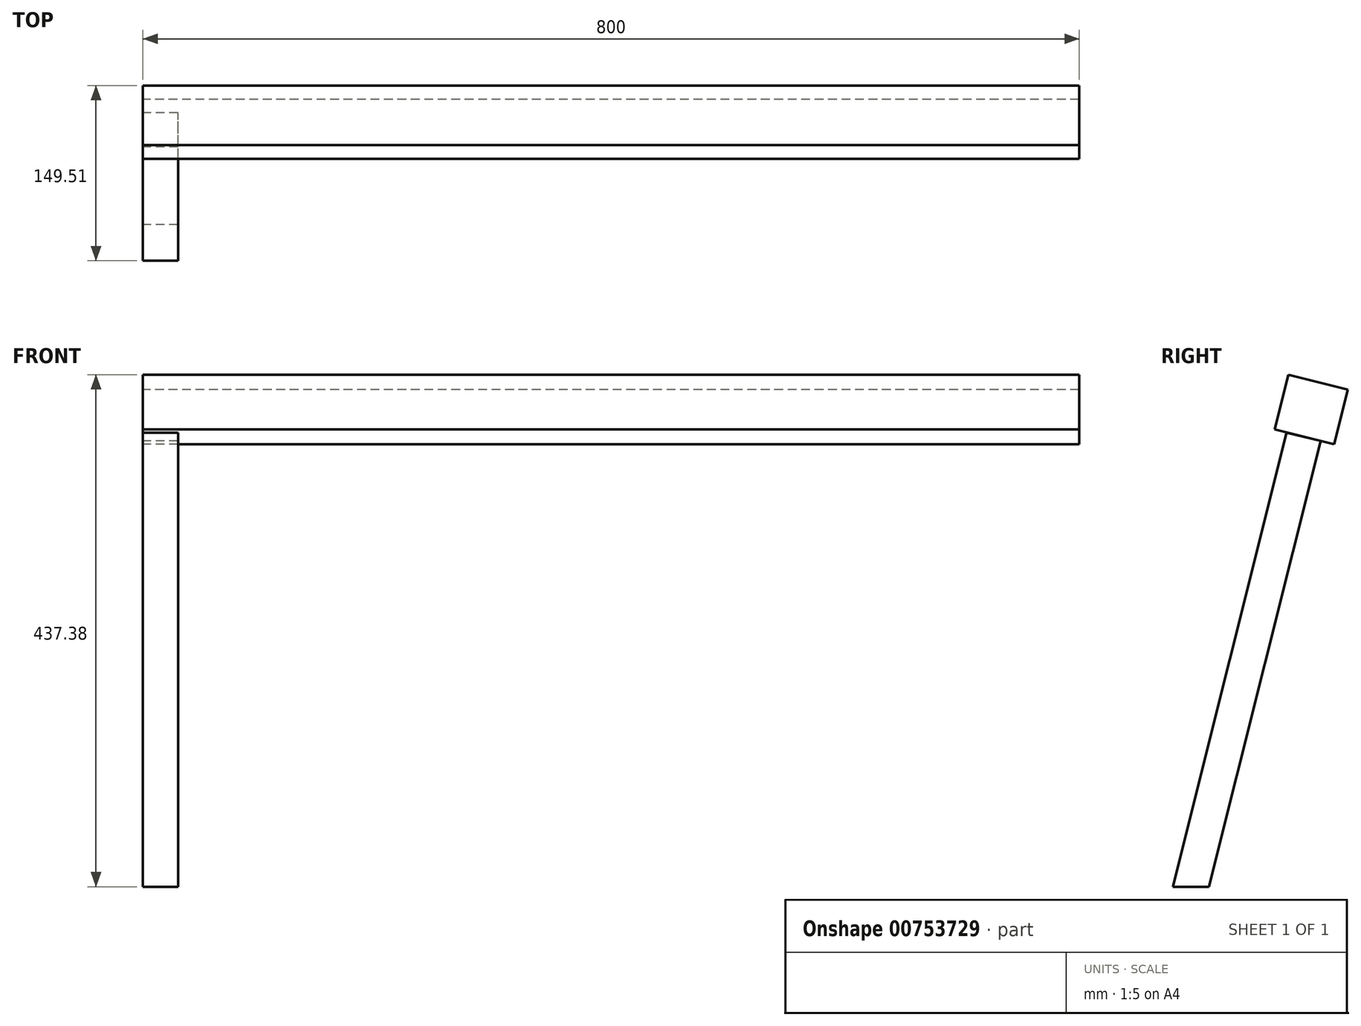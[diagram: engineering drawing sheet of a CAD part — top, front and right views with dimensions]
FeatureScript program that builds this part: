
annotation { "Feature Type Name" : "Feature", "Feature Type Description" : "" }
export const myFeature = defineFeature(function(context is Context, id is Id, definition is map)
    precondition{}
    {
        {
            var Q0;
            Q0=qCreatedBy(makeId("Right.planeOp"),FACE);
            var sketch = newSketch(context, id + "F0", { "sketchPlane" : qUnion([Q0])});
            skLineSegment(sketch, "E0", {"start": v(0, 0) * mm, "end": v(97.18, 388.02) * mm});
            skLineSegment(sketch, "E1.0", {"start": v(30.93, 0) * mm, "end": v(126.28, 380.73) * mm});
            skLineSegment(sketch, "E2", {"start": v(97.18, 388.02) * mm, "end": v(126.28, 380.73) * mm});
            skLineSegment(sketch, "E3", {"start": v(0, 0) * mm, "end": v(30.93, 0) * mm});
            skSolve(sketch);
        }
        {
            var Q0;
            Q0=makeQuery(id+"F0.imprint","IMPRINT",FACE,{"disambiguationData":[TD([[makeQuery(id+"F0.imprint","IMPRINT",EDGE,{"derivedFrom":sQuery(id+"F0.wireOp",EDGE,"E0")}),-1.0]])]});
            extrude(context, id + "F1", {"entities" : qUnion([Q0]), "depth" : 30 * mm, "offsetDistance" : 25 * mm});
        }
        {
            var Q0;
            Q0=qCreatedBy(makeId("Right.planeOp"),FACE);
            var sketch = newSketch(context, id + "F2", { "sketchPlane" : qUnion([Q0])});
            skLineSegment(sketch, "E4", {"start": v(87.04, 390.8) * mm, "end": v(137.84, 378.08) * mm});
            skLineSegment(sketch, "E5", {"start": v(87.04, 390.8) * mm, "end": v(98.7, 437.38) * mm});
            skLineSegment(sketch, "E6", {"start": v(98.7, 437.38) * mm, "end": v(149.5, 424.67) * mm});
            skLineSegment(sketch, "E7", {"start": v(137.84, 378.08) * mm, "end": v(149.5, 424.67) * mm});
            skSolve(sketch);
        }
        {
            var Q0;
            Q0 = qSketchRegion(id + "F2", true);
            extrude(context, id + "F3", {"entities" : qUnion([Q0]), "depth" : 800 * mm, "offsetDistance" : 25 * mm});
        }
    });
